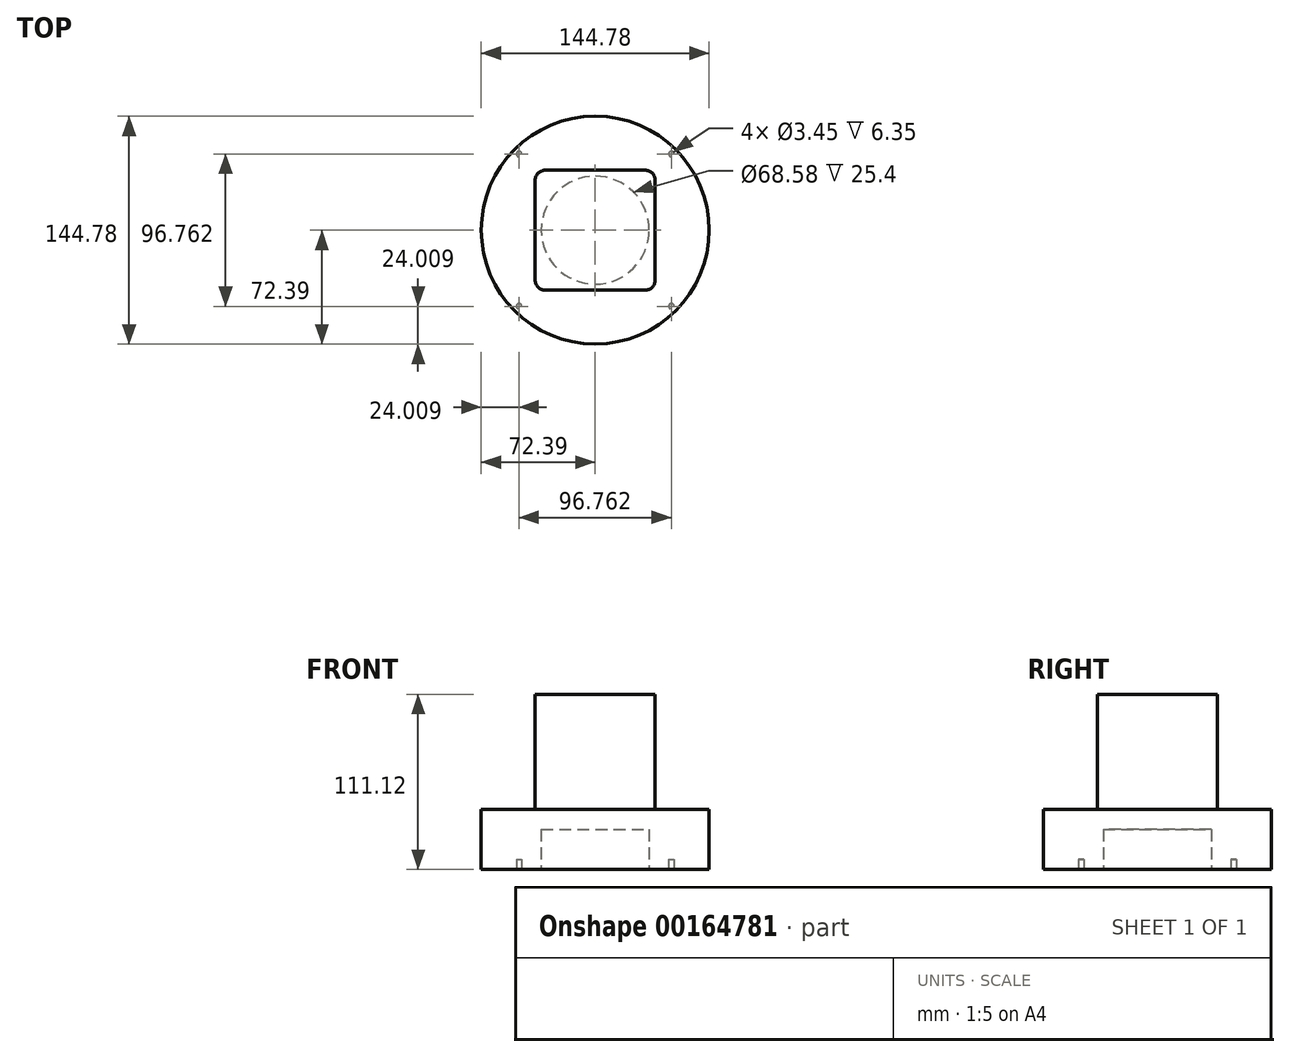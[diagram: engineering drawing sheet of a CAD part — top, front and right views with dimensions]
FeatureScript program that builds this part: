
annotation { "Feature Type Name" : "Feature", "Feature Type Description" : "" }
export const myFeature = defineFeature(function(context is Context, id is Id, definition is map)
    precondition{}
    {
        {
            var Q0;
            Q0=qCreatedBy(makeId("Top.planeOp"),FACE);
            var sketch = newSketch(context, id + "F0", { "sketchPlane" : qUnion([Q0])});
            skCircle(sketch, "E0", {"center": v(0, 0) * mm, "radius": 72.4 * mm});
            skSolve(sketch);
        }
        {
            var Q0;
            Q0 = qSketchRegion(id + "F0", true);
            extrude(context, id + "F1", {"entities" : qUnion([Q0]), "depth" : 38.1 * mm});
        }
        {
            var Q0;
            Q0=makeQuery(id+"F1.opExtrude","CAP_FACE",FACE,{"disambiguationData":[OSD([sQuery(id+"F0.wireOp",EDGE,"E0")])],"isStart":false});
            var sketch = newSketch(context, id + "F2", { "sketchPlane" : qUnion([Q0])});
            skLineSegment(sketch, "E1.bottom", {"start": v(38.1, -38.1) * mm, "end": v(-38.1, -38.1) * mm});
            skLineSegment(sketch, "E1.top", {"start": v(38.1, 38.1) * mm, "end": v(-38.1, 38.1) * mm});
            skLineSegment(sketch, "E1.left", {"start": v(38.1, -38.1) * mm, "end": v(38.1, 38.1) * mm});
            skLineSegment(sketch, "E1.right", {"start": v(-38.1, -38.1) * mm, "end": v(-38.1, 38.1) * mm});
            skPoint(sketch, "E1.middle", {"position": v(0, 0) * mm});
            skSolve(sketch);
        }
        {
            var Q0;
            Q0 = qSketchRegion(id + "F2", true);
            extrude(context, id + "F3", {"entities" : qUnion([Q0]), "operationType" : NewBodyOperationType.ADD, "depth" : 73.02 * mm});
        }
        {
            var Q0;
            Q0=makeQuery(id+"F3.opExtrude","SWEPT_EDGE",EDGE,{"disambiguationData":[OSD([sQuery(id+"F2.wireOp",EDGE,"E1.bottom"),sQuery(id+"F2.wireOp",EDGE,"E1.right")])]});
            var Q1;
            Q1=makeQuery(id+"F3.opExtrude","SWEPT_EDGE",EDGE,{"disambiguationData":[OSD([sQuery(id+"F2.wireOp",EDGE,"E1.top"),sQuery(id+"F2.wireOp",EDGE,"E1.right")])]});
            var Q2;
            Q2=makeQuery(id+"F3.opExtrude","SWEPT_EDGE",EDGE,{"disambiguationData":[OSD([sQuery(id+"F2.wireOp",EDGE,"E1.bottom"),sQuery(id+"F2.wireOp",EDGE,"E1.left")])]});
            var Q3;
            Q3=makeQuery(id+"F3.opExtrude","SWEPT_EDGE",EDGE,{"disambiguationData":[OSD([sQuery(id+"F2.wireOp",EDGE,"E1.top"),sQuery(id+"F2.wireOp",EDGE,"E1.left")])]});
            fillet(context, id + "F4", {"entities" : qUnion([Q0, Q1, Q2, Q3]), "radius" : 6.35 * mm, "tangentPropagation" : true, "allowEdgeOverflow" : false});
        }
        {
            var Q0;
            Q0=makeQuery(id+"F1.opExtrude","CAP_FACE",FACE,{"disambiguationData":[OSD([sQuery(id+"F0.wireOp",EDGE,"E0")])],"isStart":true});
            var sketch = newSketch(context, id + "F5", { "sketchPlane" : qUnion([Q0])});
            skLineSegment(sketch, "E2.bottom", {"start": v(48.38, 48.38) * mm, "end": v(-48.38, 48.38) * mm, "construction": true});
            skLineSegment(sketch, "E2.top", {"start": v(48.38, -48.38) * mm, "end": v(-48.38, -48.38) * mm, "construction": true});
            skLineSegment(sketch, "E2.left", {"start": v(48.38, 48.38) * mm, "end": v(48.38, -48.38) * mm, "construction": true});
            skLineSegment(sketch, "E2.right", {"start": v(-48.38, 48.38) * mm, "end": v(-48.38, -48.38) * mm, "construction": true});
            skPoint(sketch, "E2.middle", {"position": v(0, 0) * mm});
            skCircle(sketch, "E3", {"center": v(48.38, 48.38) * mm, "radius": 3.97 * mm, "construction": true});
            skCircle(sketch, "E4", {"center": v(-48.38, 48.38) * mm, "radius": 1.73 * mm});
            skCircle(sketch, "E5", {"center": v(-48.38, -48.38) * mm, "radius": 1.73 * mm});
            skCircle(sketch, "E6", {"center": v(48.38, -48.38) * mm, "radius": 1.73 * mm});
            skCircle(sketch, "E7", {"center": v(48.38, 48.38) * mm, "radius": 1.73 * mm});
            skSolve(sketch);
        }
        {
            var Q0;
            Q0 = qSketchRegion(id + "F5", true);
            extrude(context, id + "F6", {"entities" : qUnion([Q0]), "operationType" : NewBodyOperationType.REMOVE, "oppositeDirection" : true, "depth" : 6.35 * mm});
        }
        {
            var Q0;
            Q0=makeQuery(id+"F1.opExtrude","CAP_FACE",FACE,{"disambiguationData":[OSD([sQuery(id+"F0.wireOp",EDGE,"E0")])],"isStart":true});
            var sketch = newSketch(context, id + "F7", { "sketchPlane" : qUnion([Q0])});
            skCircle(sketch, "E8", {"center": v(0, 0) * mm, "radius": 34.3 * mm});
            skSolve(sketch);
        }
        {
            var Q0;
            Q0 = qSketchRegion(id + "F7", true);
            extrude(context, id + "F8", {"entities" : qUnion([Q0]), "operationType" : NewBodyOperationType.REMOVE, "oppositeDirection" : true, "depth" : 25.4 * mm});
        }
    });
